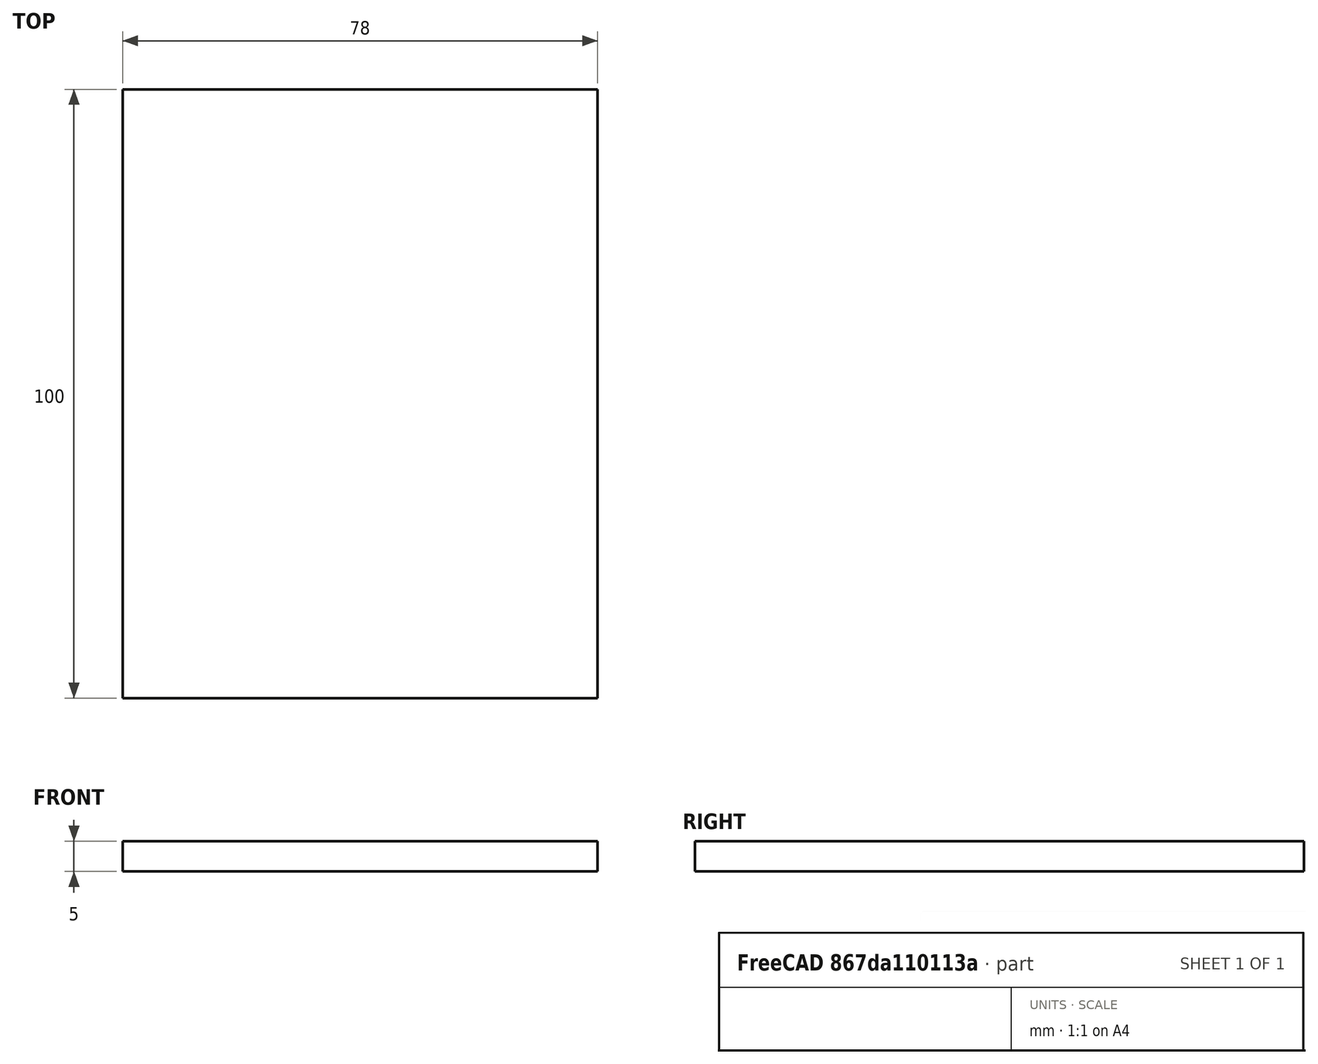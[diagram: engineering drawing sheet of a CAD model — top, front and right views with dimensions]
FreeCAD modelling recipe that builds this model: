
FCSTD DOCUMENT  (FreeCAD 0.19R24366 (Git))
Label: Deckel_raspberry_def
License: All rights reserved
LicenseURL: http://en.wikipedia.org/wiki/All_rights_reserved
objects: Sketcher::SketchObject×2, PartDesign::Pad×1, PartDesign::Body×1
note: 5 computed .brp shape members not serialized (recipe doc carries the construction recipe); baked Part::Feature solids carry a one-line shape summary decoded from their .brp

FEATURE [Sketcher::SketchObject] Sketch
  FullyConstrained = true
  MapMode = 5
  Support = -> [XY_Plane]
  sketch-geometry (4):
    g0: LineSegment StartX=-39 StartY=-50 StartZ=0 EndX=39 EndY=-50 EndZ=0
    g1: LineSegment StartX=39 StartY=-50 StartZ=0 EndX=39 EndY=50 EndZ=0
    g2: LineSegment StartX=39 StartY=50 StartZ=0 EndX=-39 EndY=50 EndZ=0
    g3: LineSegment StartX=-39 StartY=50 StartZ=0 EndX=-39 EndY=-50 EndZ=0
  constraints (11):
    c: Coincident(g0,g1)
    c: Coincident(g1,g2)
    c: Coincident(g2,g3)
    c: Coincident(g3,g0)
    c: Horizontal(g0)
    c: Horizontal(g2)
    c: Vertical(g1)
    c: Vertical(g3)
    c: DistanceX(g0,g0) = 78
    c: DistanceY(g0,g1) = 100
    c: Symmetric(g1,g0,g-1)
FEATURE [PartDesign::Pad] Pad
  Direction = (1,1,1)
  Length = 5
  Length2 = 100
  Profile = -> Sketch
  Type = 0
FEATURE [Sketcher::SketchObject] Sketch001
  FullyConstrained = true
  MapMode = 5
  Placement = pos=(0,-50,0) rot=(1,0,0;1.5708rad)
  Support = -> [Pad]
FEATURE [PartDesign::Body] Body
  Group = -> [Sketch,Pad,Sketch001]
  Origin = -> Origin
  Tip = -> Pad
